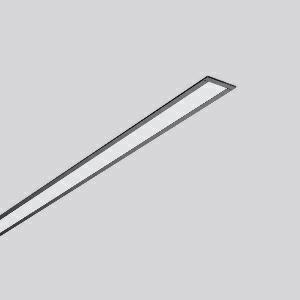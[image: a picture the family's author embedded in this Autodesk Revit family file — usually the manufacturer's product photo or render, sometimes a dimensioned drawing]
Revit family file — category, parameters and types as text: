
# Revit family: less_is_more_27_312176_003_46eb
name_source: partatom
category: Lighting Fixtures
units: mm (PartAtom-declared; Revit-internal decimal feet)

## family parameters
Cut with Voids When Loaded = No
Host = Face
Light Source = No
Part Type = Normal
Room Calculation Point = No
Round Connector Dimension = Use Diameter
Shared = No

## types (1)
- LESS IS MORE 27 (1 x LED Modul 830, 1600 lm, 3000)
    Apparent Load = 29 VA
    CIE Flux Codes = 48 79 96 100 100
    Color Rendering = 80
    Color Temperature = 3000
    Default Elevation = 1800 mm
    Description = Series: LESS IS MORE 27
Recessed ceiling and wall luminaire with slim design. Housing: extruded aluminium profile, powder-coated. End cap aluminium powder-coated. Diffuser made of non-yellowing plastic (PMMA), opal. Suitable for Recessed ceiling mounting, wall (recessed). External driver with connecting cable. 
Colour: deep black, matt (RAL 9005)
Length: 1014 mm
Width: 38 mm
Height: 2 mm
Cut-out length: 1006 mm
Cut-out width: 30 mm
Recess height: 45-60 mm
Luminaire: recess height: 37 mm
Lamp: LED
Socket: without socket
Colour temperature: 3000K
Colour rendering index (CRI): 82
System power: 29 W
Rated luminous flux: 1600 lm
Luminous efficiency: 55 lm/W
Control gear: Regulated power supply
Protection class: II
Type of protection: IP 20
    Height = 0 mm  [stored 0 ft]
    Lamp = 1 x LED Modul 830
    Lamp Light Flux = 1600 lm
    Lamp count = 1
    Length = 1014 mm
    Lifetime = 50000 h
    Luminous efficacy = 55 lm/W
    Manufacturer = RZB
    ModVariant = No
    Model = 312176.003
    Mounting Place = Ceiling, Wall
    Mounting Type = Recessed
    Number of Poles = 1
    OnlyDefault = Yes
    Power Factor = 1
    Product Name = LESS IS MORE 27
    Product group = Recessed LED linear luminaires
    ProductGroupID = 407
    Protection Class = Protection class II
    Protection Degree = IP 20
    RLX_Detail_Level = 1
    RLX_Emergency_Light_Flux = 0 lm
    RLX_Emergency_Type = 0
    RLX_Emergency_Type_DB = No
    RlxData = <blob elided: 26077 chars, md5=59290506>
    Socket = socket
    Standby Power = 0 W
    System Light Flux = 1600 lm
    System Power = 29 W
    Type Comments = Product without accessories
    Type Image = 312176.003.jpg
    URL = http://relux.com
    VarID = ---
    Voltage = 230 V
    Voltage Range = 220-240 V
    Weight = 0.00 kg
    Width = 38 mm

note: [stored X ft] marks values corroborated as IEEE doubles in the binary element streams (Revit-internal decimal feet)

## geometry (parser evidence)
native form markers: Blend x4, Sweep x10
no freeform markers — native parametric forms only
